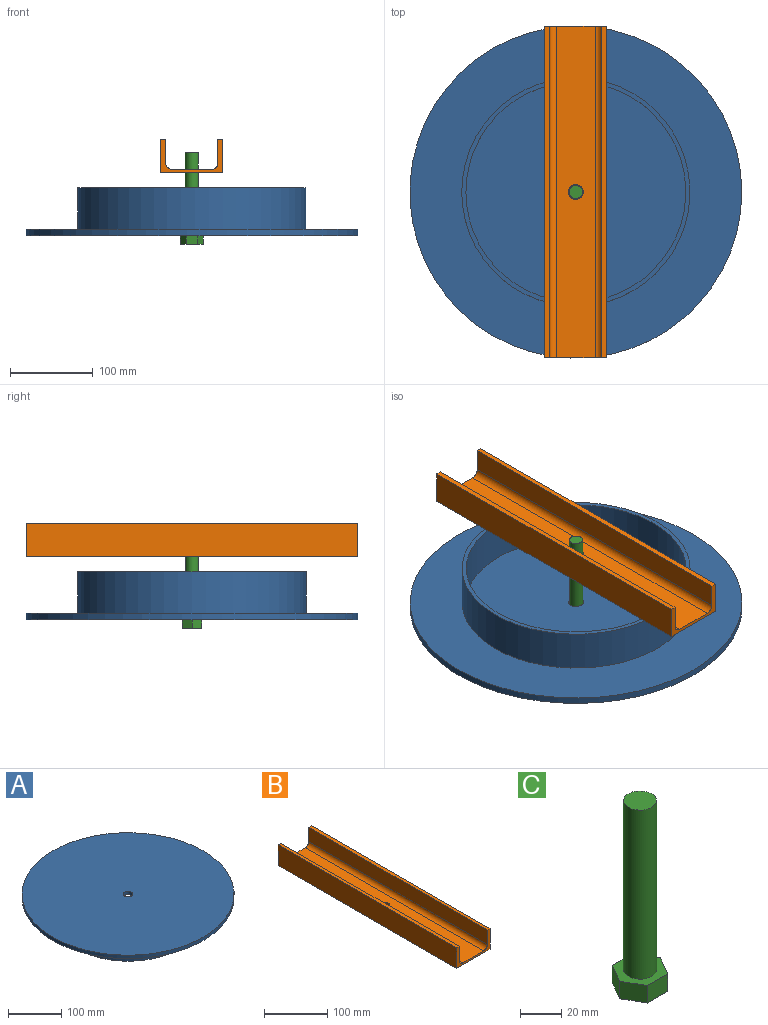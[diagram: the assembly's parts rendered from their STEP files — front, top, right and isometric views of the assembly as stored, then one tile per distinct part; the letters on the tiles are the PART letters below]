
ASSEMBLY  parts=3 mates=2
PART A: 8 faces, bbox 400x400x58 mm
  f0: plane 265x265mm, normal (0,0,-1), area 54900.1mm2, adj f1,f5
  f1: cylinder r=9mm len=18mm, axis (0,0,-1), area 452.4mm2, adj f0,f3
  f2: cylinder r=200mm len=400mm, axis (0,0,-1), area 10053.1mm2, adj f3,f4
  f3: plane 400x400mm, normal (0,0,1), area 125409.2mm2, adj f1,f2
  f4: plane 400x400mm, normal (0,0,-1), area 66268mm2, adj f2,f6
  f5: cylinder r=132.5mm len=265mm, axis (0,0,1), area 41626.1mm2, adj f0,f7
  f6: cylinder r=137.5mm len=275mm, axis (0,0,1), area 43196.9mm2, adj f4,f7
  f7: plane 275x275mm, normal (0,0,-1), area 4241.2mm2, adj f5,f6
PART B: 13 faces, bbox 75x400x40 mm
  f0: cylinder r=8mm len=400mm, axis (0,1,0), area 5026.5mm2, adj f1,f9,f10,f11
  f1: plane 400x28.2mm, normal (1,0,0), area 11280mm2, adj f0,f2,f10,f11
  f2: plane 400x6.1mm, normal (0,0,1), area 2440mm2, adj f1,f3,f10,f11
  f3: plane 400x40mm, normal (-1,0,0), area 16000mm2, adj f2,f4,f10,f11
  f4: plane 400x75mm, normal (0,0,-1), area 29745.5mm2, adj f3,f5,f10,f11,f12
  f5: plane 400x40mm, normal (1,0,0), area 16000mm2, adj f4,f6,f10,f11
  f6: plane 400x6.1mm, normal (0,0,1), area 2440mm2, adj f5,f7,f10,f11
  f7: plane 400x28.2mm, normal (-1,0,0), area 11280mm2, adj f6,f8,f10,f11
  f8: cylinder r=8mm len=400mm, axis (0,1,0), area 5026.5mm2, adj f7,f9,f10,f11
  f9: plane 400x46.8mm, normal (0,0,1), area 18465.5mm2, adj f0,f8,f10,f11,f12
  f10: plane 75x40mm, normal (0,-1,0), area 754.1mm2, adj f0,f1,f2,f3,f4,f5,f6,f7
  f11: plane 75x40mm, normal (0,1,0), area 754.1mm2, adj f0,f1,f2,f3,f4,f5,f6,f7
  f12: cylinder r=9mm len=18mm, axis (0,0,-1), area 214.9mm2, adj f4,f9
PART C: 10 faces, bbox 27.7x24x110.3 mm
  f0: cylinder r=8mm len=100mm, axis (0,0,-1), area 5026.5mm2, adj f1,f9
  f1: plane 16x16mm, normal (0,0,1), area 201.1mm2, adj f0
  f2: plane 12x10.32mm, normal (0.87,-0.5,0), area 143mm2, adj f3,f7,f8,f9
  f3: plane 12x10.32mm, normal (0.87,0.5,0), area 143mm2, adj f2,f4,f8,f9
  f4: plane 13.86x10.32mm, normal (0,1,0), area 143mm2, adj f3,f5,f8,f9
  f5: plane 12x10.32mm, normal (-0.87,0.5,0), area 143mm2, adj f4,f6,f8,f9
  f6: plane 12x10.32mm, normal (-0.87,-0.5,0), area 143mm2, adj f5,f7,f8,f9
  f7: plane 13.86x10.32mm, normal (0,-1,0), area 143mm2, adj f2,f6,f8,f9
  f8: plane 27.71x24mm, normal (0,0,-1), area 498.8mm2, adj f2,f3,f4,f5,f6,f7
  f9: plane 27.71x24mm, normal (0,0,1), area 297.7mm2, adj f0,f2,f3,f4,f5,f6,f7
PLACE A rot(axis=(-1,0,0),180deg) t=(-149.11,-100.09,-104.69)mm
PLACE B rot(axis=(0,0,1),0deg) t=(-186.61,99.91,-36.69)mm
PLACE C rot(axis=(0,0,1),0deg) t=(-149.11,-100.09,-112.69)mm
MATE pin_slot C.f0 <-> A.f2  axis (0,0,-1) through (-149.11,-100.09,-112.69)mm
MATE pin_slot A.f5 <-> B.f12  axis (0,0,1) through (-149.11,-100.09,-104.69)mm
